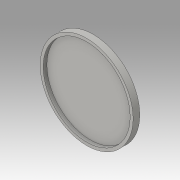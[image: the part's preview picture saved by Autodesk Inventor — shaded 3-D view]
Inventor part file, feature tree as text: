
AUTODESK INVENTOR PART (.ipt)
format: ipt  version: 2016 (Build 200138000, 138)  size: 87,552 bytes
history: native  units: in
note: dims shown in document units (in); Inventor stores cm internally (conversion verified against a paired STEP export)
features: extrude x1, shell x1, sketch x1
ambient origin geometry x8: Origin, YZ Plane, XZ Plane, XY Plane, X Axis, Y Axis, Z Axis, Center Point
bodies: Solid1 (feature_tree)
feature tree (3):
  extrude  "Extrusion1"  Depth=0.125in TaperAngle=0.0deg
  shell  "Shell1"  Thickness=0.1in
  sketch  "Sketch1"  dims[d0=2.925in d1=0.125in d2=0.0in d3=0.1in]
